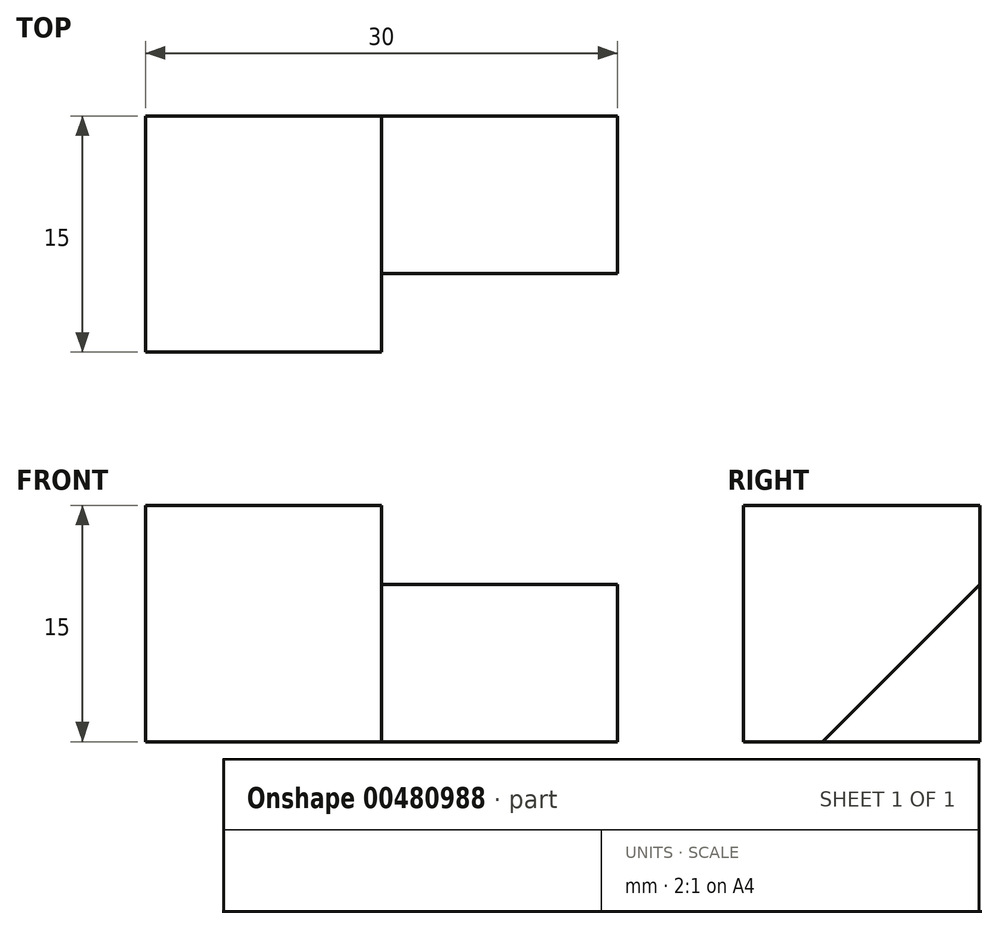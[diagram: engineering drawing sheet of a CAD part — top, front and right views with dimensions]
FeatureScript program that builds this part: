
annotation { "Feature Type Name" : "Feature", "Feature Type Description" : "" }
export const myFeature = defineFeature(function(context is Context, id is Id, definition is map)
    precondition{}
    {
        {
            var Q0;
            Q0=qCreatedBy(makeId("Top.planeOp"),FACE);
            var sketch = newSketch(context, id + "F0", { "sketchPlane" : qUnion([Q0])});
            skLineSegment(sketch, "E0.bottom", {"start": v(-15.2, -4.77) * mm, "end": v(-0.2, -4.77) * mm});
            skLineSegment(sketch, "E0.top", {"start": v(-15.2, -19.77) * mm, "end": v(-0.2, -19.77) * mm});
            skLineSegment(sketch, "E0.left", {"start": v(-15.2, -4.77) * mm, "end": v(-15.2, -19.77) * mm});
            skLineSegment(sketch, "E0.right", {"start": v(-0.2, -4.77) * mm, "end": v(-0.2, -19.77) * mm});
            skSolve(sketch);
        }
        {
            var Q0;
            Q0=makeQuery(id+"F0.imprint","IMPRINT",FACE,{"disambiguationData":[TD([[makeQuery(id+"F0.imprint","IMPRINT",EDGE,{"derivedFrom":sQuery(id+"F0.wireOp",EDGE,"E0.bottom")}),-1.0]])]});
            extrude(context, id + "F1", {"entities" : qUnion([Q0]), "depth" : 15 * mm});
        }
        {
            var Q0;
            Q0=makeQuery(id+"F1.opExtrude","SWEPT_FACE",FACE,{"disambiguationData":[OSD([sQuery(id+"F0.wireOp",EDGE,"E0.right")])]});
            var sketch = newSketch(context, id + "F2", { "sketchPlane" : qUnion([Q0])});
            skLineSegment(sketch, "E1", {"start": v(-4.77, 0) * mm, "end": v(-4.77, 10) * mm});
            skLineSegment(sketch, "E2", {"start": v(-4.77, 0) * mm, "end": v(-14.77, 0) * mm});
            skLineSegment(sketch, "E3", {"start": v(-4.77, 10) * mm, "end": v(-14.77, 0) * mm});
            skSolve(sketch);
        }
        {
            var Q0;
            Q0=makeQuery(id+"F2.imprint","IMPRINT",FACE,{"disambiguationData":[TD([[makeQuery(id+"F2.imprint","IMPRINT",EDGE,{"derivedFrom":sQuery(id+"F2.wireOp",EDGE,"E1")}),-1.0]])]});
            extrude(context, id + "F3", {"entities" : qUnion([Q0]), "operationType" : NewBodyOperationType.ADD, "depth" : 15 * mm});
        }
    });
